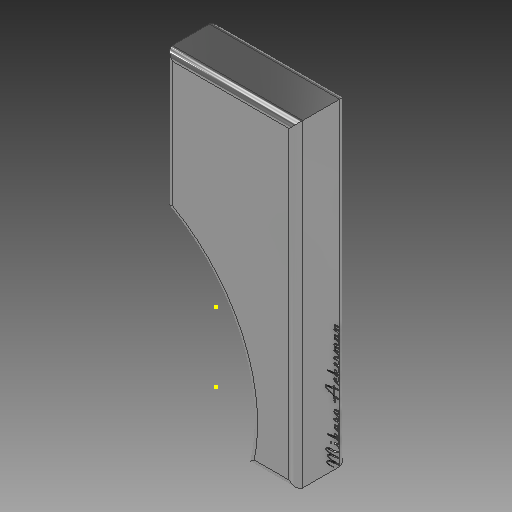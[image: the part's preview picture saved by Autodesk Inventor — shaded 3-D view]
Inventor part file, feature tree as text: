
AUTODESK INVENTOR PART (.ipt)
format: ipt  version: 2021 (Build 250183000, 183)  size: 1,173,504 bytes
history: native  units: mm
features: sketch x8, extrude x5, fillet x4, emboss x1
ambient origin geometry x8: Origin, YZ Plane, XZ Plane, XY Plane, X Axis, Y Axis, Z Axis, Center Point
bodies: Solid1 (feature_tree)
feature tree (18):
  extrude  "Extrusion1"  Depth=18.946mm
  fillet  "Fillet1"  Radius=19.781mm
  sketch  "Sketch2"  dims[d3=7.285mm d4=7.366mm d5=0.0mm d6=1.0mm]
  extrude  "Extrusion2"  Depth=7.366mm TaperAngle=0.0deg
  fillet  "Fillet2"  Radius=1.0mm
  extrude  "Extrusion3"  Depth=1.21mm
  fillet  "Fillet3"  Radius=1.21mm
  sketch  "Sketch5"  dims[d13=0.25mm d14=0.4mm d15=0.8mm]
  extrude  "Extrusion4"  Depth=10.16mm TaperAngle=0.0deg
  extrude  "Extrusion5"  Depth=0.4mm
  fillet  "Fillet4"  Radius=0.8mm
  emboss  "Emboss1"
  sketch  "Sketch1"  dims[d0=46.274mm d1=18.946mm d2=19.781mm]
  sketch  "Sketch3"  dims[d7=1.21mm d8=1.21mm d9=1.21mm]
  sketch  "Sketch4"  dims[d10=1.21mm d11=10.16mm d12=0.0mm]
  sketch  "Sketch6"  dims[d16=1.1mm]
  sketch  "Sketch7"  dims[d17=2.2mm]
  sketch  "Sketch8"  dims[d18=0.8mm d19=1.1mm d20=0.4mm d21=2.2mm d22=10.16mm d23=0.0mm d24=0.15mm d25=2.0mm d26=1.7mm d28=2.0mm d29=0.3mm d30=10.16mm d31=0.0mm d32=0.4mm d33=0.4mm d34=0.4mm d35=0.4mm d36=10.16mm d37=0.0mm d38=0.15mm d39=1.0mm d40=0.0mm]
